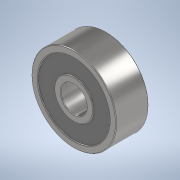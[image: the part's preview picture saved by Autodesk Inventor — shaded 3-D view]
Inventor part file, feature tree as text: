
AUTODESK INVENTOR PART (.ipt)
format: ipt  version: 2020 (Build 240168000, 168)  size: 179,200 bytes
history: native  units: mm
features: extrude x2, sketch x1, fillet x1
ambient origin geometry x8: Origin, YZ Plane, XZ Plane, XY Plane, X Axis, Y Axis, Z Axis, Center Point
bodies: Solid1 (feature_tree)
feature tree (4):
  sketch  "Sketch1"  dims[d0=4.0mm d1=13.0mm d2=1.0mm d3=1.0mm d4=5.0mm d5=0.0mm d6=4.8mm d7=0.0mm d8=0.1mm]
  extrude  "Extrusion1"  Depth=0.1mm
  extrude  "Extrusion2"  Depth=0.1mm
  fillet  "Fillet1"  Radius=1.0mm
